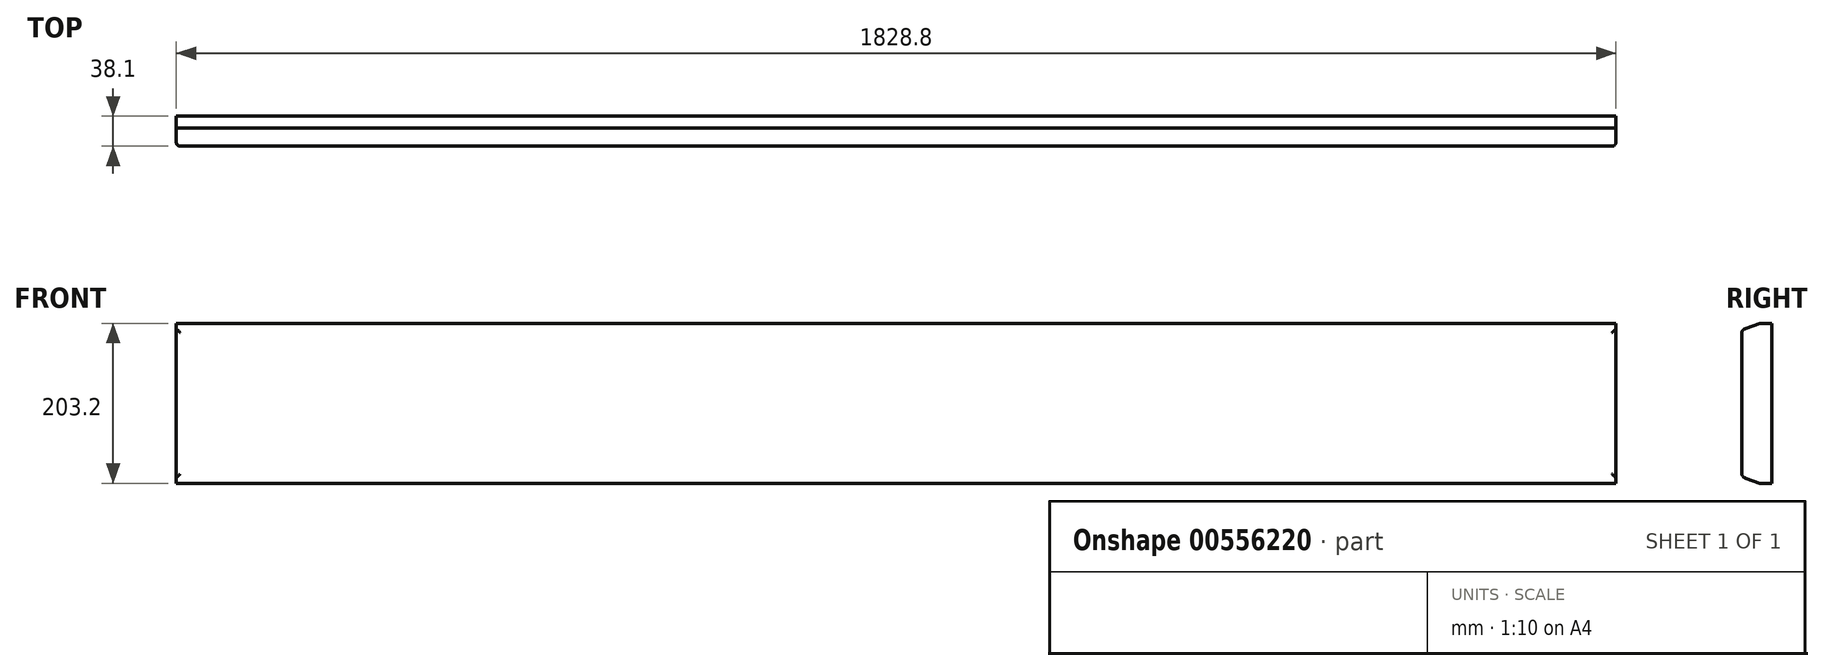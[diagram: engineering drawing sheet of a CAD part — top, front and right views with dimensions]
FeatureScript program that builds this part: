
annotation { "Feature Type Name" : "Feature", "Feature Type Description" : "" }
export const myFeature = defineFeature(function(context is Context, id is Id, definition is map)
    precondition{}
    {
        {
            var Q0;
            Q0=qCreatedBy(makeId("Front.planeOp"),FACE);
            var sketch = newSketch(context, id + "F0", { "sketchPlane" : qUnion([Q0])});
            skLineSegment(sketch, "E0.bottom", {"start": v(-961.95, 101.6) * mm, "end": v(866.85, 101.6) * mm});
            skLineSegment(sketch, "E0.top", {"start": v(-961.95, -101.6) * mm, "end": v(866.85, -101.6) * mm});
            skLineSegment(sketch, "E0.left", {"start": v(-961.95, 101.6) * mm, "end": v(-961.95, -101.6) * mm});
            skLineSegment(sketch, "E0.right", {"start": v(866.85, 101.6) * mm, "end": v(866.85, -101.6) * mm});
            skPoint(sketch, "E0.middle", {"position": v(-47.55, 0) * mm});
            skSolve(sketch);
        }
        {
            var Q0;
            Q0=makeQuery(id+"F0.imprint","IMPRINT",FACE,{"disambiguationData":[TD([[makeQuery(id+"F0.imprint","IMPRINT",EDGE,{"derivedFrom":sQuery(id+"F0.wireOp",EDGE,"E0.bottom")}),-1.0]])]});
            extrude(context, id + "F1", {"entities" : qUnion([Q0]), "depth" : 38.1 * mm, "offsetDistance" : 25.4 * mm});
        }
        {
            var Q0;
            Q0=makeQuery(id+"F1.opExtrude","CAP_EDGE",EDGE,{"disambiguationData":[OSD([sQuery(id+"F0.wireOp",EDGE,"E0.bottom")])],"isStart":false});
            chamfer(context, id + "F2", {"entities" : qUnion([Q0]), "chamferType" : ChamferType.OFFSET_ANGLE, "width" : 22.86 * mm, "oppositeDirection" : false, "angle" : 20 * degree, "tangentPropagation" : true});
        }
        {
            var Q0;
            Q0=makeQuery(id+"F1.opExtrude","CAP_EDGE",EDGE,{"disambiguationData":[OSD([sQuery(id+"F0.wireOp",EDGE,"E0.top")])],"isStart":false});
            chamfer(context, id + "F3", {"entities" : qUnion([Q0]), "chamferType" : ChamferType.OFFSET_ANGLE, "width" : 22.86 * mm, "oppositeDirection" : true, "angle" : 20 * degree, "tangentPropagation" : true});
        }
        {
            var Q0;
            Q0=makeQuery(id+"F1.opExtrude","CAP_FACE",FACE,{"disambiguationData":[OSD([sQuery(id+"F0.wireOp",EDGE,"E0.bottom"),sQuery(id+"F0.wireOp",EDGE,"E0.top"),sQuery(id+"F0.wireOp",EDGE,"E0.left"),sQuery(id+"F0.wireOp",EDGE,"E0.right")])],"isStart":false});
            fillet(context, id + "F4", {"entities" : qUnion([Q0]), "radius" : 5.08 * mm, "tangentPropagation" : true, "allowEdgeOverflow" : false});
        }
    });
